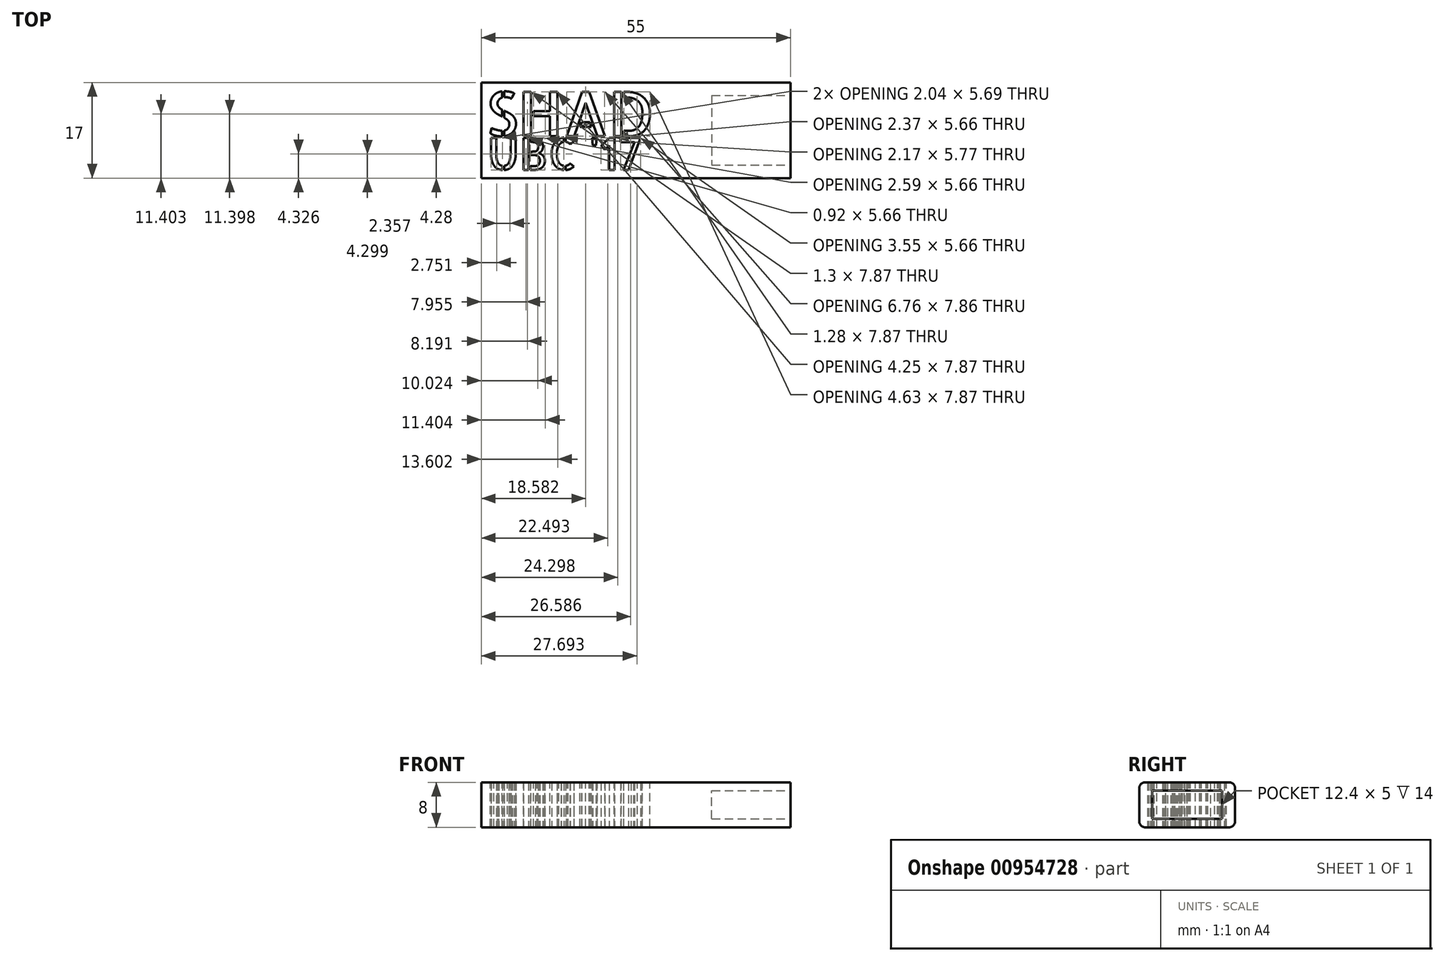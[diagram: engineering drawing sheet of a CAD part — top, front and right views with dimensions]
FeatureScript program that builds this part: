
annotation { "Feature Type Name" : "Feature", "Feature Type Description" : "" }
export const myFeature = defineFeature(function(context is Context, id is Id, definition is map)
    precondition{}
    {
        {
            var Q0;
            Q0=qCreatedBy(makeId("Front.planeOp"),FACE);
            var sketch = newSketch(context, id + "F0", { "sketchPlane" : qUnion([Q0])});
            skLineSegment(sketch, "E0.bottom", {"start": v(7.5, -4) * mm, "end": v(-7.5, -4) * mm});
            skLineSegment(sketch, "E0.top", {"start": v(7.5, 4) * mm, "end": v(-7.5, 4) * mm});
            skLineSegment(sketch, "E0.left", {"start": v(8.5, -3) * mm, "end": v(8.5, 3) * mm});
            skLineSegment(sketch, "E0.right", {"start": v(-8.5, -3) * mm, "end": v(-8.5, 3) * mm});
            skPoint(sketch, "E0.middle", {"position": v(0, 0) * mm});
            skPoint(sketch, "E1.visualSharp", {"position": v(-8.5, 4) * mm});
            skArc(sketch, "E1.filletArc", {"start": v(-7.5, 4) * mm, "mid": v(-8.2, 3.7) * mm, "end": v(-8.5, 3) * mm});
            skPoint(sketch, "E2.visualSharp", {"position": v(-8.5, -4) * mm});
            skArc(sketch, "E2.filletArc", {"start": v(-8.5, -3) * mm, "mid": v(-8.2, -3.7) * mm, "end": v(-7.5, -4) * mm});
            skPoint(sketch, "E3.visualSharp", {"position": v(8.5, -4) * mm});
            skArc(sketch, "E3.filletArc", {"start": v(7.5, -4) * mm, "mid": v(8.2, -3.7) * mm, "end": v(8.5, -3) * mm});
            skPoint(sketch, "E4.visualSharp", {"position": v(8.5, 4) * mm});
            skArc(sketch, "E4.filletArc", {"start": v(8.5, 3) * mm, "mid": v(8.2, 3.7) * mm, "end": v(7.5, 4) * mm});
            skSolve(sketch);
        }
        {
            var Q0;
            Q0=qSketchRegion(id+"F0",true);
            extrude(context, id + "F1", {"entities" : qUnion([Q0]), "depth" : 55 * mm, "offsetDistance" : 25 * mm});
        }
        {
            var Q0;
            Q0=makeQuery(id+"F1.opExtrude","CAP_FACE",FACE,{"disambiguationData":[OSD([sQuery(id+"F0.wireOp",EDGE,"E0.bottom"),sQuery(id+"F0.wireOp",EDGE,"E0.top"),sQuery(id+"F0.wireOp",EDGE,"E0.left"),sQuery(id+"F0.wireOp",EDGE,"E0.right"),sQuery(id+"F0.wireOp",EDGE,"E1.filletArc"),sQuery(id+"F0.wireOp",EDGE,"E2.filletArc"),sQuery(id+"F0.wireOp",EDGE,"E3.filletArc"),sQuery(id+"F0.wireOp",EDGE,"E4.filletArc")])],"isStart":false});
            var sketch = newSketch(context, id + "F2", { "sketchPlane" : qUnion([Q0])});
            skLineSegment(sketch, "E5.bottom", {"start": v(6.2, -2.5) * mm, "end": v(-6.2, -2.5) * mm});
            skLineSegment(sketch, "E5.top", {"start": v(6.2, 2.5) * mm, "end": v(-6.2, 2.5) * mm});
            skLineSegment(sketch, "E5.left", {"start": v(6.2, -2.5) * mm, "end": v(6.2, 2.5) * mm});
            skLineSegment(sketch, "E5.right", {"start": v(-6.2, -2.5) * mm, "end": v(-6.2, 2.5) * mm});
            skPoint(sketch, "E5.middle", {"position": v(0, 0) * mm});
            skSolve(sketch);
        }
        {
            var Q0;
            Q0=makeQuery(id+"F2.imprint","IMPRINT",FACE,{"disambiguationData":[TD([[makeQuery(id+"F2.imprint","IMPRINT",EDGE,{"derivedFrom":sQuery(id+"F2.wireOp",EDGE,"E5.bottom")}),-1.0]])]});
            extrude(context, id + "F3", {"entities" : qUnion([Q0]), "operationType" : NewBodyOperationType.REMOVE, "oppositeDirection" : true, "depth" : 14 * mm, "offsetDistance" : 25 * mm});
        }
        {
            var Q0;
            Q0=makeQuery(id+"F1.opExtrude","SWEPT_BODY",BODY,{"disambiguationData":[OSD([sQuery(id+"F0.wireOp",EDGE,"E0.bottom"),sQuery(id+"F0.wireOp",EDGE,"E0.top"),sQuery(id+"F0.wireOp",EDGE,"E0.left"),sQuery(id+"F0.wireOp",EDGE,"E0.right"),sQuery(id+"F0.wireOp",EDGE,"E1.filletArc"),sQuery(id+"F0.wireOp",EDGE,"E2.filletArc"),sQuery(id+"F0.wireOp",EDGE,"E3.filletArc"),sQuery(id+"F0.wireOp",EDGE,"E4.filletArc")])]});
            var Q1;
            Q1=makeQuery(id+"F1.opExtrude","CAP_EDGE",EDGE,{"disambiguationData":[OSD([sQuery(id+"F0.wireOp",EDGE,"E0.left")])],"isStart":true});
            transform(context, id + "F4", {"entities" : qUnion([Q0]), "transformType" : TransformType.ROTATION, "transformAxis" : qUnion([Q1]), "angle" : 90 * degree, "makeCopy" : false});
        }
        {
            var Q0;
            Q0=qCreatedBy(makeId("Top.planeOp"),FACE);
            var sketch = newSketch(context, id + "F5", { "sketchPlane" : qUnion([Q0])});
            skText(sketch, "E6", { "text": "SHAD", "fontName": "AllertaStencil-Regular.ttf"});
            const initialGuessF5  = {"E6": [0.00925, -0.00953, 1, 0, 0.00787]};
            skSetInitialGuess(sketch, initialGuessF5);
            skSolve(sketch);
        }
        {
            var Q0;
            Q0=qCreatedBy(makeId("Top.planeOp"),FACE);
            var sketch = newSketch(context, id + "F6", { "sketchPlane" : qUnion([Q0])});
            skText(sketch, "E7", { "text": "UBC \'17", "fontName": "AllertaStencil-Regular.ttf"});
            const initialGuessF6  = {"E7": [0.0096, -0.01553, 1, 0, 0.00566]};
            skSetInitialGuess(sketch, initialGuessF6);
            skSolve(sketch);
        }
        {
            var Q0;
            Q0=qSketchRegion(id+"F5",true);
            extrude(context, id + "F7", {"entities" : qUnion([Q0]), "operationType" : NewBodyOperationType.REMOVE, "oppositeDirection" : true, "depth" : 25 * mm, "offsetDistance" : 25 * mm, "hasSecondDirection" : true, "secondDirectionOppositeDirection" : false, "secondDirectionDepth" : 25 * mm});
        }
        {
            var Q0;
            Q0=qSketchRegion(id+"F6",true);
            extrude(context, id + "F8", {"entities" : qUnion([Q0]), "operationType" : NewBodyOperationType.REMOVE, "depth" : 25 * mm, "offsetDistance" : 25 * mm, "hasSecondDirection" : true, "secondDirectionOppositeDirection" : true, "secondDirectionDepth" : 25 * mm});
        }
    });
